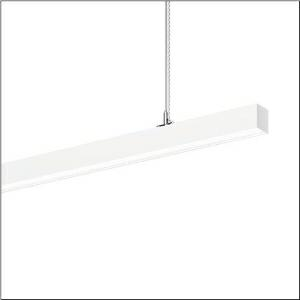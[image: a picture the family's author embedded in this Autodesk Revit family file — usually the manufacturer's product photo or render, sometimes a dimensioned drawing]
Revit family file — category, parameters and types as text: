
# Revit family: silica_21_51mx33da37wb
name_source: partatom
category: Lighting Fixtures
units: mm (PartAtom-declared; Revit-internal decimal feet)

## family parameters
Cut with Voids When Loaded = No
Host = Face
Light Source = No
Part Type = Normal
Room Calculation Point = No
Round Connector Dimension = Use Diameter
Shared = No

## types (1)
- --- (1 x LED, 5910 lm, 41.3 W, 3000K)
    Apparent Load = 41 VA
    CIE Flux Codes = 78 96 99 55 100
    Color Rendering = 80
    Color Temperature = 3000K
    Default Elevation = 1800 mm
    Description = Silica 21, office luminaire, primary optical cover: prismatic diffuser, of PMMA, CAT 2 (L<= 3000cd/m²), light emission: direct/indirect distribution, primary light characteristic: symmetric, installation type: suspended mounting, LED, rated luminous flux: 5.910lm, luminous efficacy: 143lm/W, light colour: 830, colour temperature: 3000K, control gear: DALI 2, with terminal, 3+2-pole, max. 2.5mm², mains connection: 220..240V, AC, 50/60Hz, rated input power: 41.3W, luminaire housing, of aluminium, traffic white (RAL 9016), length: 1.204mm, width: 53mm, height: 53mm, protection rating (complete): IP20, insulation class (complete): insulation class I (protective earthing), certification: CE, permissible operating ambient temperature: 0..+35°C, standard: EN 50419, packaging unit: 1 piece
    Height = 53 mm
    Lamp = 1 x LED
    Lamp Light Flux = 5910 lm
    Lamp Power = 41.3 W
    Lamp count = 1
    Length = 1204 mm
    Luminous efficacy = 143 lm/W
    Manufacturer = Siteco
    ModVariant = No
    Model = 51MX33DA37WB
    Mounting Place = Ceiling
    Mounting Type = Pendant
    Number of Poles = 1
    OnlyDefault = Yes
    Power Factor = 1
    Product Name = Silica 21
    Product group = office luminaire | ceiling pendant
    ProductGroupID = 903
    Protection Class = Protection class I
    Protection Degree = IP 20
    RLX_Detail_Level = 1
    RLX_Emergency_Light_Flux = 0 lm
    RLX_Emergency_Type = 0
    RLX_Emergency_Type_DB = No
    RlxData = <blob elided: 21417 chars, md5=08537a11>
    Socket = socket
    Standby Power = 0 W
    System Light Flux = 5910 lm
    System Power = 41 W
    Type Comments = factory setting: luminous flux: 100 % | dim-lin: 254 | 345 mA
    Type Image = l_1349007.jpg
    URL = http://relux.com
    VarID = @adj_119045
    Voltage = 0 V
    Weight = 0.00 kg
    Width = 53 mm

## geometry (parser evidence)
native form markers: Blend x4, Sweep x14
no freeform markers — native parametric forms only
